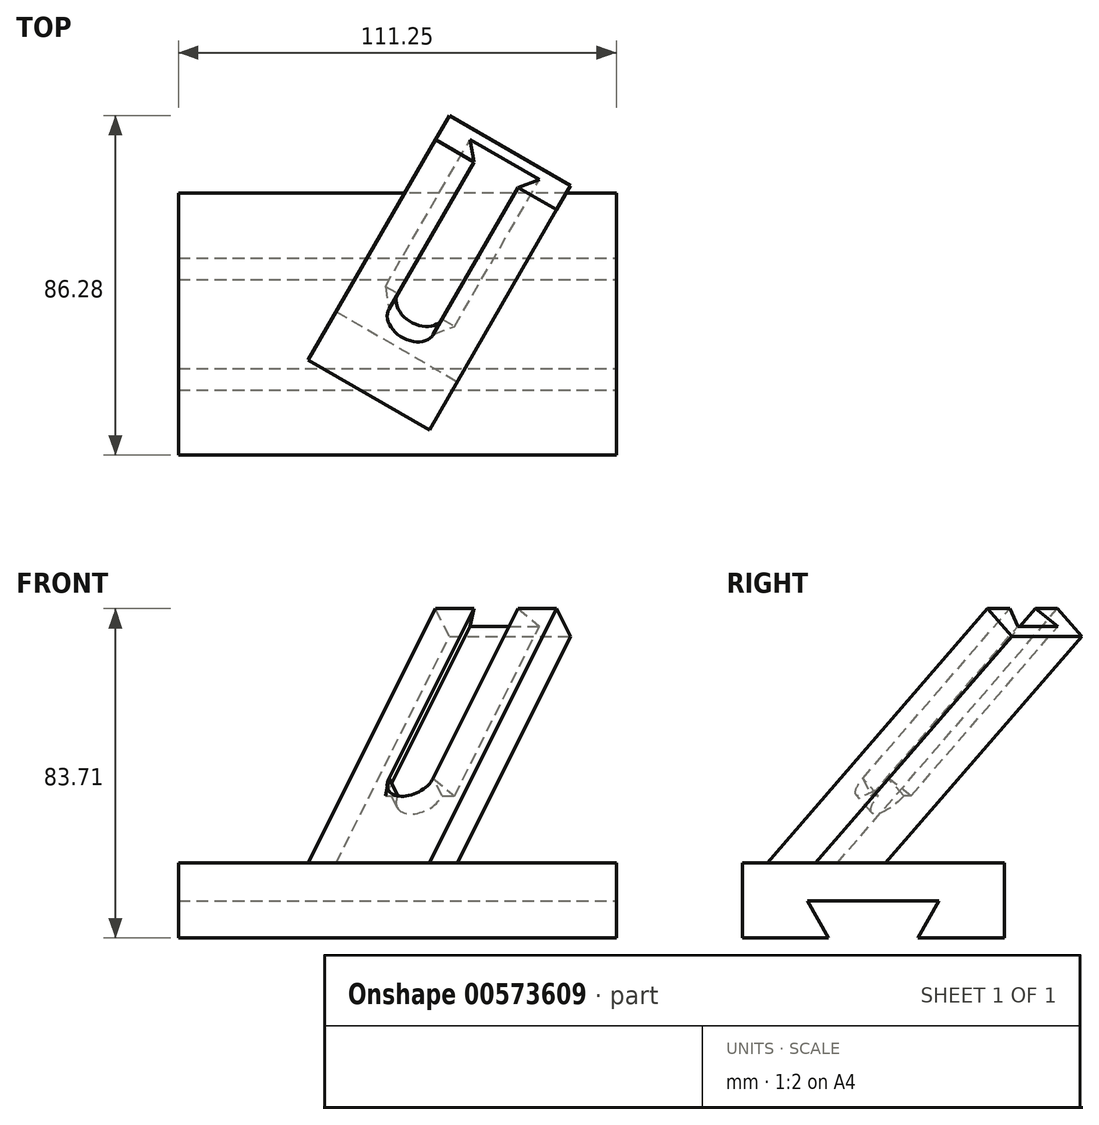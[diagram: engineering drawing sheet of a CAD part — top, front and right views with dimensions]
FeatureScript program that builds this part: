
annotation { "Feature Type Name" : "Feature", "Feature Type Description" : "" }
export const myFeature = defineFeature(function(context is Context, id is Id, definition is map)
    precondition{}
    {
        {
            var Q0;
            Q0=qCreatedBy(makeId("Front.planeOp"),FACE);
            var sketch = newSketch(context, id + "F0", { "sketchPlane" : qUnion([Q0])});
            skLineSegment(sketch, "E0.bottom", {"start": v(0, 0) * mm, "end": v(-111.25, 0) * mm});
            skLineSegment(sketch, "E0.top", {"start": v(0, -19.05) * mm, "end": v(-111.25, -19.05) * mm});
            skLineSegment(sketch, "E0.left", {"start": v(0, 0) * mm, "end": v(0, -19.05) * mm});
            skLineSegment(sketch, "E0.right", {"start": v(-111.25, 0) * mm, "end": v(-111.25, -19.05) * mm});
            skSolve(sketch);
        }
        {
            var Q0;
            Q0 = qSketchRegion(id + "F0", true);
            extrude(context, id + "F1", {"entities" : qUnion([Q0]), "endBound" : BoundingType.SYMMETRIC, "oppositeDirection" : true, "depth" : 66.55 * mm, "offsetDistance" : 25.4 * mm});
        }
        {
            var Q0;
            Q0=qCreatedBy(makeId("Right.planeOp"),FACE);
            var sketch = newSketch(context, id + "F2", { "sketchPlane" : qUnion([Q0])});
            skLineSegment(sketch, "E1.0", {"start": v(33.27, -19.05) * mm, "end": v(-33.27, -19.05) * mm});
            skLineSegment(sketch, "E2.bottom", {"start": v(16.76, -19.05) * mm, "end": v(-16.76, -19.05) * mm});
            skLineSegment(sketch, "E2.top", {"start": v(16.76, -9.65) * mm, "end": v(-16.76, -9.65) * mm});
            skPoint(sketch, "E2.middle", {"position": v(0, -14.35) * mm});
            skLineSegment(sketch, "E3", {"start": v(16.76, -9.65) * mm, "end": v(11.34, -19.05) * mm});
            skLineSegment(sketch, "E4", {"start": v(-16.76, -9.65) * mm, "end": v(-11.34, -19.05) * mm});
            skSolve(sketch);
        }
        {
            var Q0;
            Q0 = qSketchRegion(id + "F2", true);
            extrude(context, id + "F3", {"entities" : qUnion([Q0]), "operationType" : NewBodyOperationType.REMOVE, "endBound" : BoundingType.THROUGH_ALL, "oppositeDirection" : true, "depth" : 25.4 * mm, "offsetDistance" : 25.4 * mm});
        }
        {
            var Q0;
            Q0=qCreatedBy(makeId("Top.planeOp"),FACE);
            var sketch = newSketch(context, id + "F4", { "sketchPlane" : qUnion([Q0])});
            skLineSegment(sketch, "E5.0", {"start": v(0, -33.27) * mm, "end": v(-111.25, -33.27) * mm});
            skLineSegment(sketch, "E6", {"start": v(-77.79, -26.92) * mm, "end": v(-47.5, -26.92) * mm, "construction": true});
            skLineSegment(sketch, "E7", {"start": v(-47.5, -26.92) * mm, "end": v(-78.3, -9.14) * mm});
            skLineSegment(sketch, "E8", {"start": v(-78.3, -9.14) * mm, "end": v(-71.18, 3.17) * mm});
            skLineSegment(sketch, "E9", {"start": v(-71.18, 3.17) * mm, "end": v(-40.39, -14.6) * mm});
            skLineSegment(sketch, "E10", {"start": v(-40.39, -14.6) * mm, "end": v(-47.5, -26.92) * mm});
            skSolve(sketch);
        }
        {
            var Q0;
            Q0=makeQuery(id+"F4.imprint","IMPRINT",FACE,{"disambiguationData":[TD([[makeQuery(id+"F4.imprint","IMPRINT",EDGE,{"derivedFrom":sQuery(id+"F4.wireOp",EDGE,"E7")}),-1.0]])]});
            var Q1;
            Q1=sQuery(id+"F4.wireOp",EDGE,"E7");
            revolve(context, id + "F5", {"operationType" : NewBodyOperationType.ADD, "entities" : qUnion([Q0]), "axis" : qUnion([Q1]), "revolveType" : RevolveType.TWO_DIRECTIONS, "oppositeDirection" : true, "angle" : 45 * degree, "angleBack" : 360 * degree});
        }
        {
            var Q0;
            Q0=makeQuery(id+"F5.opRevolve","SWEPT_FACE",FACE,{"disambiguationData":[OSD([sQuery(id+"F4.wireOp",EDGE,"E10")])]});
            var sketch = newSketch(context, id + "F6", { "sketchPlane" : qUnion([Q0])});
            skPoint(sketch, "E11", {"position": v(-47.07, 0) * mm});
            skLineSegment(sketch, "E12", {"start": v(-47.07, 0) * mm, "end": v(17.6, 64.66) * mm});
            skLineSegment(sketch, "E13", {"start": v(-47.07, 0) * mm, "end": v(-32.84, 0) * mm});
            skLineSegment(sketch, "E14", {"start": v(-32.84, 0) * mm, "end": v(31.82, 64.66) * mm});
            skLineSegment(sketch, "E15", {"start": v(31.82, 64.66) * mm, "end": v(17.6, 64.66) * mm});
            skSolve(sketch);
        }
        {
            var Q0;
            Q0 = qSketchRegion(id + "F6", true);
            extrude(context, id + "F7", {"entities" : qUnion([Q0]), "operationType" : NewBodyOperationType.ADD, "oppositeDirection" : true, "depth" : 35.56 * mm, "offsetDistance" : 25.4 * mm});
        }
        {
            var Q0;
            Q0=makeQuery(id+"F7.boolean.opBoolean","MERGE",FACE,{"derivedFrom":[makeQuery(id+"F5.opRevolve","SWEPT_FACE",FACE,{"disambiguationData":[OSD([sQuery(id+"F4.wireOp",EDGE,"E10")])]}),makeQuery(id+"F7.opExtrude","CAP_FACE",FACE,{"disambiguationData":[OSD([sQuery(id+"F6.wireOp",EDGE,"E12"),sQuery(id+"F6.wireOp",EDGE,"E13"),sQuery(id+"F6.wireOp",EDGE,"E14"),sQuery(id+"F6.wireOp",EDGE,"E15")])],"isStart":true})]});
            var sketch = newSketch(context, id + "F8", { "sketchPlane" : qUnion([Q0])});
            skPoint(sketch, "E16.0", {"position": v(17.6, 64.66) * mm});
            skLineSegment(sketch, "E17", {"start": v(17.6, 64.66) * mm, "end": v(24.7, 57.55) * mm});
            skSolve(sketch);
        }
        {
            var Q0;
            {var subQ0=sQuery(id+"F8.wireOp",EDGE,"E17");Q0=makeQuery(id+"F8.imprint","IMPRINT",FACE,{"disambiguationData":[TD([[makeQuery(id+"F8.imprint","IMPRINT",EDGE,{"derivedFrom":subQ0}),1.0]])]});}
            extrude(context, id + "F9", {"entities" : qUnion([Q0]), "operationType" : NewBodyOperationType.REMOVE, "endBound" : BoundingType.THROUGH_ALL, "oppositeDirection" : true, "depth" : 25.4 * mm, "offsetDistance" : 25.4 * mm});
        }
        {
            var Q0;
            Q0=makeQuery(id+"F9.boolean.opBoolean","COPY",FACE,{"derivedFrom":makeQuery(id+"F9.opExtrude","SWEPT_FACE",FACE,{"disambiguationData":[OSD([sQuery(id+"F8.wireOp",EDGE,"E17")])]})});
            var sketch = newSketch(context, id + "F10", { "sketchPlane" : qUnion([Q0])});
            skPoint(sketch, "E18.0", {"position": v(-54.66, -13.63) * mm});
            skLineSegment(sketch, "E19", {"start": v(-64.07, -9.8) * mm, "end": v(-61.67, -3.91) * mm});
            skLineSegment(sketch, "E20", {"start": v(-61.67, -3.91) * mm, "end": v(-42.85, -11.6) * mm});
            skLineSegment(sketch, "E21", {"start": v(-42.85, -11.6) * mm, "end": v(-45.25, -17.47) * mm});
            skLineSegment(sketch, "E22", {"start": v(-45.25, -17.47) * mm, "end": v(-64.07, -9.8) * mm});
            skLineSegment(sketch, "E23", {"start": v(-48.65, -16.09) * mm, "end": v(-42.85, -11.6) * mm});
            skLineSegment(sketch, "E24", {"start": v(-61.67, -3.91) * mm, "end": v(-60.67, -11.18) * mm});
            skSolve(sketch);
        }
        {
            var Q0;
            Q0=makeQuery(id+"F10.imprint","IMPRINT",FACE,{"disambiguationData":[TD([[makeQuery(id+"F10.imprint","IMPRINT",EDGE,{"derivedFrom":sQuery(id+"F10.wireOp",EDGE,"E20")}),-1.0]])]});
            extrude(context, id + "F11", {"entities" : qUnion([Q0]), "operationType" : NewBodyOperationType.REMOVE, "oppositeDirection" : true, "depth" : 60.96 * mm, "offsetDistance" : 25.4 * mm});
        }
        {
            var Q0;
            Q0=makeQuery(id+"F7.boolean.opBoolean","MERGE",FACE,{"derivedFrom":[makeQuery(id+"F5.opRevolve","CAP_FACE",FACE,{"disambiguationData":[OSD([sQuery(id+"F4.wireOp",EDGE,"E7"),sQuery(id+"F4.wireOp",EDGE,"E8"),sQuery(id+"F4.wireOp",EDGE,"E9"),sQuery(id+"F4.wireOp",EDGE,"E10")])],"isStart":false}),makeQuery(id+"F7.opExtrude","SWEPT_FACE",FACE,{"disambiguationData":[OSD([sQuery(id+"F6.wireOp",EDGE,"E12")])]})]});
            var sketch = newSketch(context, id + "F12", { "sketchPlane" : qUnion([Q0])});
            skLineSegment(sketch, "E25.0", {"start": v(-49.15, 17.04) * mm, "end": v(-37.13, 12.13) * mm});
            skArc(sketch, "E26", {"start": v(-49.15, 17.04) * mm, "mid": v(-45.6, 8.57) * mm, "end": v(-37.13, 12.13) * mm});
            skSolve(sketch);
        }
        {
            var Q0;
            Q0=makeQuery(id+"F12.imprint","IMPRINT",FACE,{"disambiguationData":[TD([[makeQuery(id+"F12.imprint","IMPRINT",EDGE,{"derivedFrom":sQuery(id+"F12.wireOp",EDGE,"E25.0")}),-1.0]])]});
            extrude(context, id + "F13", {"entities" : qUnion([Q0]), "operationType" : NewBodyOperationType.REMOVE, "oppositeDirection" : true, "depth" : 6.35 * mm, "offsetDistance" : 25.4 * mm});
        }
    });
